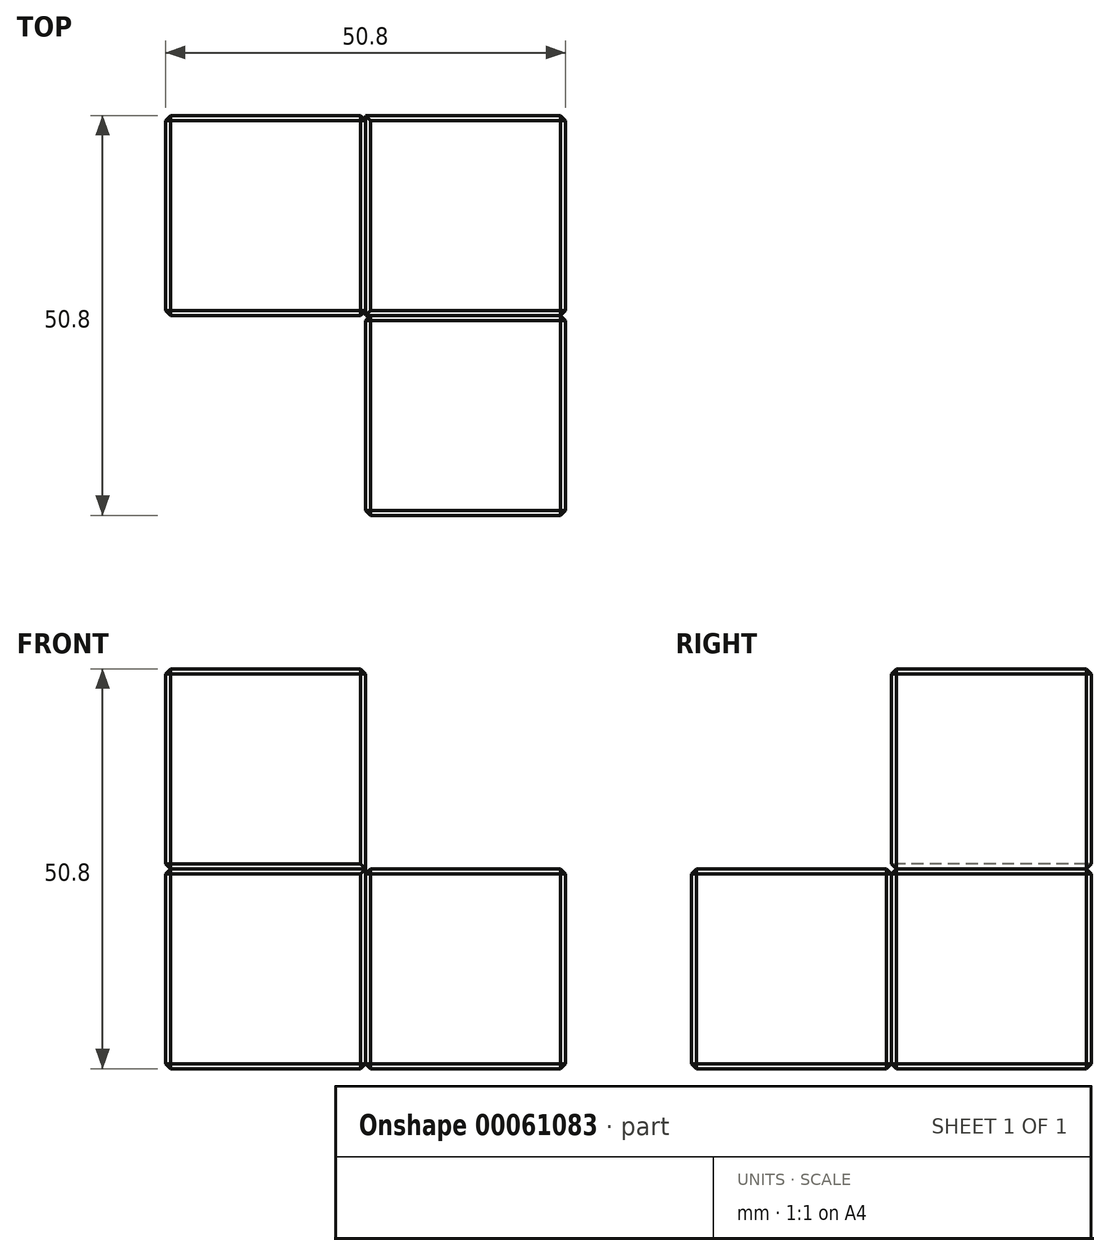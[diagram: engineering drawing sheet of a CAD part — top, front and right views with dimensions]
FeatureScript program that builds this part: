
annotation { "Feature Type Name" : "Feature", "Feature Type Description" : "" }
export const myFeature = defineFeature(function(context is Context, id is Id, definition is map)
    precondition{}
    {
        {
            var Q0;
            Q0=qCreatedBy(makeId("Top.planeOp"),FACE);
            var sketch = newSketch(context, id + "F0", { "sketchPlane" : qUnion([Q0])});
            skLineSegment(sketch, "E0.rect.bottom", {"start": v(-12.7, 12.7) * mm, "end": v(12.7, 12.7) * mm});
            skLineSegment(sketch, "E0.rect.top", {"start": v(-12.7, -12.7) * mm, "end": v(12.7, -12.7) * mm});
            skLineSegment(sketch, "E0.rect.left", {"start": v(-12.7, 12.7) * mm, "end": v(-12.7, -12.7) * mm});
            skLineSegment(sketch, "E0.rect.right", {"start": v(12.7, 12.7) * mm, "end": v(12.7, -12.7) * mm});
            skPoint(sketch, "E0.rect.middle", {"position": v(0, 0) * mm});
            skLineSegment(sketch, "E1.bottom", {"start": v(-12.7, 12.7) * mm, "end": v(-38.1, 12.7) * mm});
            skLineSegment(sketch, "E1.top", {"start": v(-12.7, -12.7) * mm, "end": v(-38.1, -12.7) * mm});
            skLineSegment(sketch, "E1.right", {"start": v(-38.1, 12.7) * mm, "end": v(-38.1, -12.7) * mm});
            skLineSegment(sketch, "E2.top", {"start": v(-12.7, -38.1) * mm, "end": v(12.7, -38.1) * mm});
            skLineSegment(sketch, "E2.left", {"start": v(-12.7, -12.7) * mm, "end": v(-12.7, -38.1) * mm});
            skLineSegment(sketch, "E2.right", {"start": v(12.7, -12.7) * mm, "end": v(12.7, -38.1) * mm});
            skSolve(sketch);
        }
        {
            var Q0;
            Q0=makeQuery(id+"F0.imprint","IMPRINT",FACE,{"disambiguationData":[TD([[makeQuery(id+"F0.imprint","IMPRINT",EDGE,{"derivedFrom":sQuery(id+"F0.wireOp",EDGE,"E1.bottom")}),1.0]])]});
            extrude(context, id + "F1", {"entities" : qUnion([Q0]), "depth" : 25.4 * mm});
        }
        {
            var Q0;
            Q0=makeQuery(id+"F0.imprint","IMPRINT",FACE,{"disambiguationData":[TD([[makeQuery(id+"F0.imprint","IMPRINT",EDGE,{"derivedFrom":sQuery(id+"F0.wireOp",EDGE,"E0.rect.bottom")}),-1.0]])]});
            extrude(context, id + "F2", {"entities" : qUnion([Q0]), "depth" : 25.4 * mm});
        }
        {
            var Q0;
            Q0=makeQuery(id+"F0.imprint","IMPRINT",FACE,{"disambiguationData":[TD([[makeQuery(id+"F0.imprint","IMPRINT",EDGE,{"derivedFrom":sQuery(id+"F0.wireOp",EDGE,"E0.rect.top")}),-1.0]])]});
            extrude(context, id + "F3", {"entities" : qUnion([Q0]), "depth" : 25.4 * mm});
        }
        {
            var Q0;
            Q0=makeQuery(id+"F1.opExtrude","CAP_FACE",FACE,{"disambiguationData":[OSD([sQuery(id+"F0.wireOp",EDGE,"E1.bottom"),sQuery(id+"F0.wireOp",EDGE,"E1.top"),sQuery(id+"F0.wireOp",EDGE,"E0.rect.left"),sQuery(id+"F0.wireOp",EDGE,"E1.right")])],"isStart":false});
            extrude(context, id + "F4", {"entities" : qUnion([Q0]), "depth" : 25.4 * mm});
        }
        {
            var Q0;
            Q0=makeQuery(id+"F4.opExtrude","CAP_FACE",FACE,{"disambiguationData":[OSD([sQuery(id+"F0.wireOp",EDGE,"E1.bottom"),sQuery(id+"F0.wireOp",EDGE,"E1.top"),sQuery(id+"F0.wireOp",EDGE,"E0.rect.left"),sQuery(id+"F0.wireOp",EDGE,"E1.right")])],"isStart":false});
            var Q1;
            Q1=makeQuery(id+"F4.opExtrude","SWEPT_FACE",FACE,{"disambiguationData":[OSD([sQuery(id+"F0.wireOp",EDGE,"E1.top")])]});
            var Q2;
            Q2=makeQuery(id+"F1.opExtrude","SWEPT_FACE",FACE,{"disambiguationData":[OSD([sQuery(id+"F0.wireOp",EDGE,"E1.top")])]});
            var Q3;
            Q3=makeQuery(id+"F2.opExtrude","CAP_FACE",FACE,{"disambiguationData":[OSD([sQuery(id+"F0.wireOp",EDGE,"E0.rect.bottom"),sQuery(id+"F0.wireOp",EDGE,"E0.rect.right"),sQuery(id+"F0.wireOp",EDGE,"E0.rect.left"),sQuery(id+"F0.wireOp",EDGE,"E0.rect.top")])],"isStart":false});
            var Q4;
            Q4=makeQuery(id+"F3.opExtrude","CAP_FACE",FACE,{"disambiguationData":[OSD([sQuery(id+"F0.wireOp",EDGE,"E0.rect.top"),sQuery(id+"F0.wireOp",EDGE,"E2.top"),sQuery(id+"F0.wireOp",EDGE,"E2.left"),sQuery(id+"F0.wireOp",EDGE,"E2.right")])],"isStart":false});
            var Q5;
            Q5=makeQuery(id+"F3.opExtrude","SWEPT_FACE",FACE,{"disambiguationData":[OSD([sQuery(id+"F0.wireOp",EDGE,"E2.left")])]});
            var Q6;
            Q6=makeQuery(id+"F1.opExtrude","SWEPT_FACE",FACE,{"disambiguationData":[OSD([sQuery(id+"F0.wireOp",EDGE,"E1.right")])]});
            var Q7;
            Q7=makeQuery(id+"F4.opExtrude","SWEPT_FACE",FACE,{"disambiguationData":[OSD([sQuery(id+"F0.wireOp",EDGE,"E1.right")])]});
            var Q8;
            Q8=makeQuery(id+"F3.opExtrude","SWEPT_FACE",FACE,{"disambiguationData":[OSD([sQuery(id+"F0.wireOp",EDGE,"E2.right")])]});
            var Q9;
            Q9=makeQuery(id+"F2.opExtrude","SWEPT_FACE",FACE,{"disambiguationData":[OSD([sQuery(id+"F0.wireOp",EDGE,"E0.rect.right")])]});
            var Q10;
            Q10=makeQuery(id+"F2.opExtrude","CAP_FACE",FACE,{"disambiguationData":[OSD([sQuery(id+"F0.wireOp",EDGE,"E0.rect.bottom"),sQuery(id+"F0.wireOp",EDGE,"E0.rect.right"),sQuery(id+"F0.wireOp",EDGE,"E0.rect.left"),sQuery(id+"F0.wireOp",EDGE,"E0.rect.top")])],"isStart":true});
            var Q11;
            Q11=makeQuery(id+"F1.opExtrude","CAP_FACE",FACE,{"disambiguationData":[OSD([sQuery(id+"F0.wireOp",EDGE,"E1.bottom"),sQuery(id+"F0.wireOp",EDGE,"E1.top"),sQuery(id+"F0.wireOp",EDGE,"E0.rect.left"),sQuery(id+"F0.wireOp",EDGE,"E1.right")])],"isStart":true});
            var Q12;
            Q12=makeQuery(id+"F3.opExtrude","CAP_FACE",FACE,{"disambiguationData":[OSD([sQuery(id+"F0.wireOp",EDGE,"E0.rect.top"),sQuery(id+"F0.wireOp",EDGE,"E2.top"),sQuery(id+"F0.wireOp",EDGE,"E2.left"),sQuery(id+"F0.wireOp",EDGE,"E2.right")])],"isStart":true});
            var Q13;
            Q13=makeQuery(id+"F1.opExtrude","SWEPT_FACE",FACE,{"disambiguationData":[OSD([sQuery(id+"F0.wireOp",EDGE,"E1.bottom")])]});
            var Q14;
            Q14=makeQuery(id+"F4.opExtrude","SWEPT_FACE",FACE,{"disambiguationData":[OSD([sQuery(id+"F0.wireOp",EDGE,"E1.bottom")])]});
            chamfer(context, id + "F5", {"entities" : qUnion([Q0, Q1, Q2, Q3, Q4, Q5, Q6, Q7, Q8, Q9, Q10, Q11, Q12, Q13, Q14]), "width" : 0.64 * mm, "tangentPropagation" : true});
        }
    });
